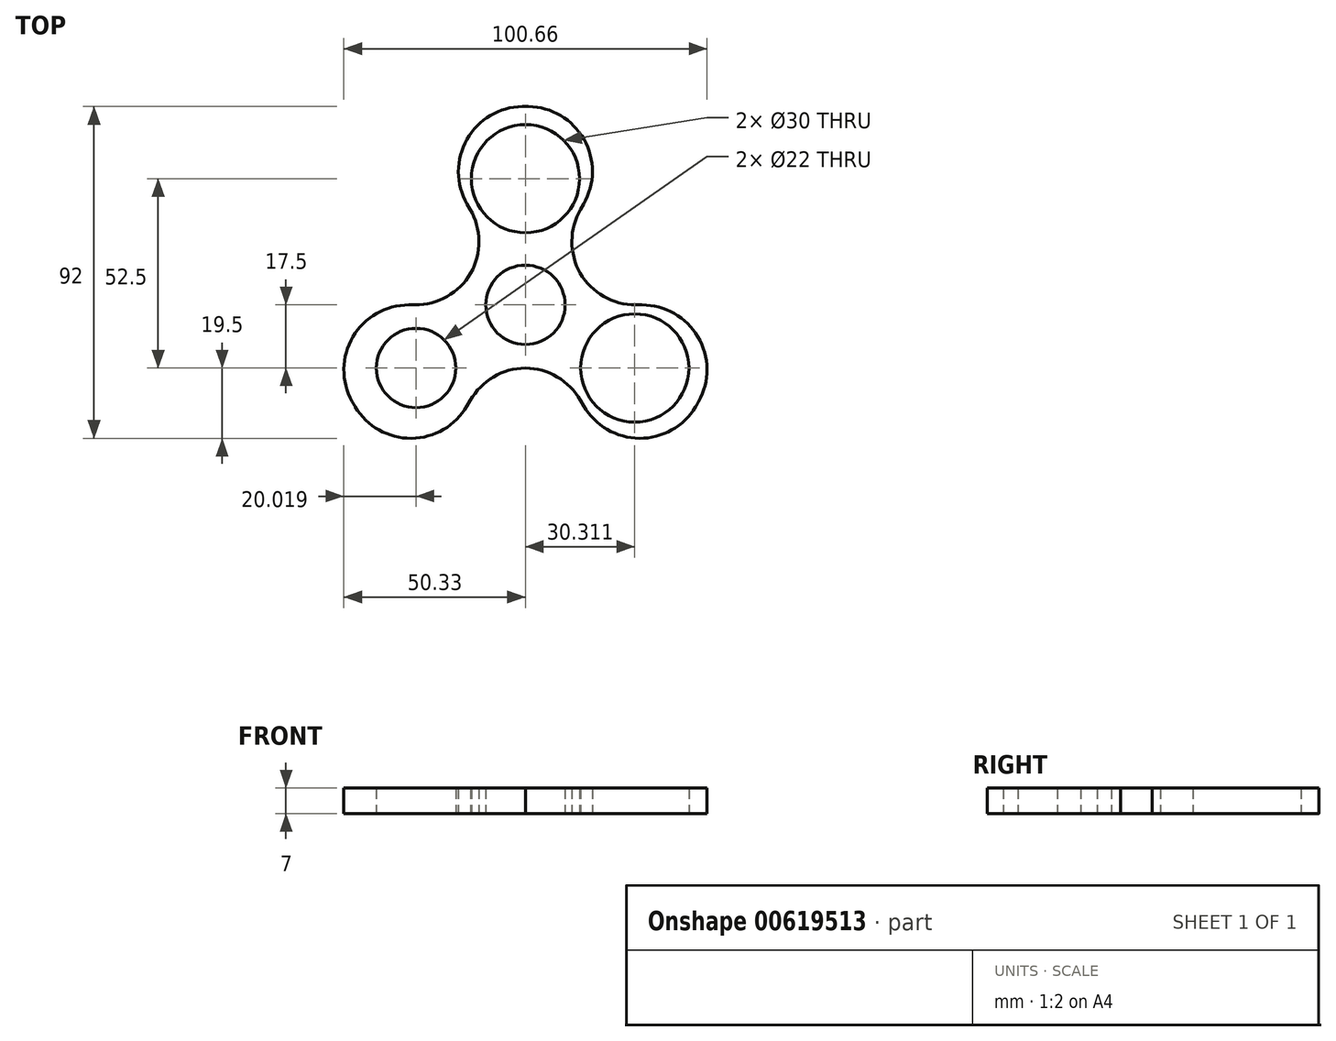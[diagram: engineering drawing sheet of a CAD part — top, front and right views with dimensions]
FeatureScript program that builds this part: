
annotation { "Feature Type Name" : "Feature", "Feature Type Description" : "" }
export const myFeature = defineFeature(function(context is Context, id is Id, definition is map)
    precondition{}
    {
        {
            var Q0;
            Q0=qCreatedBy(makeId("Top.planeOp"),FACE);
            var sketch = newSketch(context, id + "F0", { "sketchPlane" : qUnion([Q0])});
            skCircle(sketch, "E0", {"center": v(0, 0) * mm, "radius": 11 * mm});
            skCircle(sketch, "E1", {"center": v(0, 0) * mm, "radius": 15 * mm});
            skLineSegment(sketch, "E2", {"start": v(0, 11) * mm, "end": v(0, 55) * mm});
            skLineSegment(sketch, "E3.1.0", {"start": v(-5.5, 9.53) * mm, "end": v(-27.5, 47.63) * mm});
            skLineSegment(sketch, "E3.2.0", {"start": v(-9.53, 5.5) * mm, "end": v(-47.63, 27.5) * mm});
            skLineSegment(sketch, "E4.1.3.0", {"start": v(-11, 0) * mm, "end": v(-55, 0) * mm});
            skLineSegment(sketch, "E4.1.4.0", {"start": v(-9.53, -5.5) * mm, "end": v(-47.63, -27.5) * mm});
            skLineSegment(sketch, "E4.1.5.0", {"start": v(-5.5, -9.53) * mm, "end": v(-27.5, -47.63) * mm});
            skCircle(sketch, "E5", {"center": v(0, 0) * mm, "radius": 55 * mm});
            skLineSegment(sketch, "E6.1.6.0", {"start": v(0, -11) * mm, "end": v(0, -55) * mm});
            skLineSegment(sketch, "E6.1.7.0", {"start": v(5.5, -9.53) * mm, "end": v(27.5, -47.63) * mm});
            skLineSegment(sketch, "E6.1.8.0", {"start": v(9.53, -5.5) * mm, "end": v(47.63, -27.5) * mm});
            skLineSegment(sketch, "E6.1.9.0", {"start": v(11, 0) * mm, "end": v(55, 0) * mm});
            skLineSegment(sketch, "E6.1.10.0", {"start": v(9.53, 5.5) * mm, "end": v(47.63, 27.5) * mm});
            skLineSegment(sketch, "E6.1.11.0", {"start": v(5.5, 9.53) * mm, "end": v(27.5, 47.63) * mm});
            skCircle(sketch, "E7", {"center": v(-30.31, -17.5) * mm, "radius": 15 * mm});
            skCircle(sketch, "E8.1.0", {"center": v(30.31, -17.5) * mm, "radius": 15 * mm});
            skCircle(sketch, "E8.2.0", {"center": v(0, 35) * mm, "radius": 15 * mm});
            skCircle(sketch, "E9", {"center": v(-30.31, -17.5) * mm, "radius": 11 * mm});
            skCircle(sketch, "E10.1.0", {"center": v(30.31, -17.5) * mm, "radius": 11 * mm});
            skCircle(sketch, "E10.2.0", {"center": v(0, 35) * mm, "radius": 11 * mm});
            skCircle(sketch, "E11", {"center": v(0, 0) * mm, "radius": 17.5 * mm});
            skSolve(sketch);
        }
        {
            var Q0;
            Q0=makeQuery(id+"F0.imprint","IMPRINT",FACE,{"disambiguationData":[TD([[makeQuery(id+"F0.imprint","IMPRINT",EDGE,{"derivedFrom":sQuery(id+"F0.wireOp",EDGE,"E0")}),-1.0]])]});
            var Q1;
            {var subQ0=sQuery(id+"F0.wireOp",EDGE,"E4.1.5.0");var subQ1=sQuery(id+"F0.wireOp",EDGE,"E1");var subQ2=makeQuery(id+"F0.imprint","INTERSECT",VERTEX,{"derivedFrom":[subQ1,subQ0]});Q1=makeQuery(id+"F0.imprint","IMPRINT",FACE,{"disambiguationData":[TD([[makeQuery(id+"F0.imprint","IMPRINT",EDGE,{"disambiguationData":[TD([[subQ2,1.0]])],"derivedFrom":subQ1}),-1.0]])]});}
            var Q2;
            {var subQ0=sQuery(id+"F0.wireOp",EDGE,"E2");var subQ1=sQuery(id+"F0.wireOp",EDGE,"E1");var subQ2=makeQuery(id+"F0.imprint","INTERSECT",VERTEX,{"derivedFrom":[subQ1,subQ0]});Q2=makeQuery(id+"F0.imprint","IMPRINT",FACE,{"disambiguationData":[TD([[makeQuery(id+"F0.imprint","IMPRINT",EDGE,{"disambiguationData":[TD([[subQ2,-1.0]])],"derivedFrom":subQ1}),-1.0]])]});}
            var Q3;
            {var subQ0=sQuery(id+"F0.wireOp",EDGE,"E6.1.11.0");var subQ1=sQuery(id+"F0.wireOp",EDGE,"E1");var subQ2=makeQuery(id+"F0.imprint","INTERSECT",VERTEX,{"derivedFrom":[subQ1,subQ0]});Q3=makeQuery(id+"F0.imprint","IMPRINT",FACE,{"disambiguationData":[TD([[makeQuery(id+"F0.imprint","IMPRINT",EDGE,{"disambiguationData":[TD([[subQ2,-1.0]])],"derivedFrom":subQ1}),-1.0]])]});}
            var Q4;
            {var subQ0=sQuery(id+"F0.wireOp",EDGE,"E4.1.3.0");var subQ1=sQuery(id+"F0.wireOp",EDGE,"E1");var subQ2=makeQuery(id+"F0.imprint","INTERSECT",VERTEX,{"derivedFrom":[subQ1,subQ0]});Q4=makeQuery(id+"F0.imprint","IMPRINT",FACE,{"disambiguationData":[TD([[makeQuery(id+"F0.imprint","IMPRINT",EDGE,{"disambiguationData":[TD([[subQ2,-1.0]])],"derivedFrom":subQ1}),-1.0]])]});}
            var Q5;
            {var subQ0=sQuery(id+"F0.wireOp",EDGE,"E6.1.9.0");var subQ1=sQuery(id+"F0.wireOp",EDGE,"E1");var subQ2=makeQuery(id+"F0.imprint","INTERSECT",VERTEX,{"derivedFrom":[subQ1,subQ0]});Q5=makeQuery(id+"F0.imprint","IMPRINT",FACE,{"disambiguationData":[TD([[makeQuery(id+"F0.imprint","IMPRINT",EDGE,{"disambiguationData":[TD([[subQ2,1.0]])],"derivedFrom":subQ1}),-1.0]])]});}
            var Q6;
            {var subQ0=sQuery(id+"F0.wireOp",EDGE,"E6.1.7.0");var subQ1=sQuery(id+"F0.wireOp",EDGE,"E1");var subQ2=makeQuery(id+"F0.imprint","INTERSECT",VERTEX,{"derivedFrom":[subQ1,subQ0]});Q6=makeQuery(id+"F0.imprint","IMPRINT",FACE,{"disambiguationData":[TD([[makeQuery(id+"F0.imprint","IMPRINT",EDGE,{"disambiguationData":[TD([[subQ2,-1.0]])],"derivedFrom":subQ1}),-1.0]])]});}
            var Q7;
            {var subQ0=sQuery(id+"F0.wireOp",EDGE,"E7");var subQ1=sQuery(id+"F0.wireOp",EDGE,"E4.1.4.0");var subQ2=makeQuery(id+"F0.imprint","INTERSECT",VERTEX,{"disambiguationData":[OD(0.0)],"derivedFrom":[subQ1,subQ0]});Q7=makeQuery(id+"F0.imprint","IMPRINT",FACE,{"disambiguationData":[TD([[makeQuery(id+"F0.imprint","IMPRINT",EDGE,{"disambiguationData":[TD([[subQ2,-1.0]])],"derivedFrom":subQ1}),-1.0]])]});}
            var Q8;
            {var subQ0=sQuery(id+"F0.wireOp",EDGE,"E8.1.0");var subQ1=sQuery(id+"F0.wireOp",EDGE,"E6.1.8.0");var subQ2=makeQuery(id+"F0.imprint","INTERSECT",VERTEX,{"disambiguationData":[OD(0.0)],"derivedFrom":[subQ1,subQ0]});Q8=makeQuery(id+"F0.imprint","IMPRINT",FACE,{"disambiguationData":[TD([[makeQuery(id+"F0.imprint","IMPRINT",EDGE,{"disambiguationData":[TD([[subQ2,-1.0]])],"derivedFrom":subQ1}),1.0]])]});}
            var Q9;
            {var subQ0=sQuery(id+"F0.wireOp",EDGE,"E8.1.0");var subQ1=sQuery(id+"F0.wireOp",EDGE,"E6.1.8.0");var subQ2=makeQuery(id+"F0.imprint","INTERSECT",VERTEX,{"disambiguationData":[OD(0.0)],"derivedFrom":[subQ1,subQ0]});Q9=makeQuery(id+"F0.imprint","IMPRINT",FACE,{"disambiguationData":[TD([[makeQuery(id+"F0.imprint","IMPRINT",EDGE,{"disambiguationData":[TD([[subQ2,-1.0]])],"derivedFrom":subQ1}),-1.0]])]});}
            var Q10;
            {var subQ0=sQuery(id+"F0.wireOp",EDGE,"E8.2.0");var subQ1=sQuery(id+"F0.wireOp",EDGE,"E2");var subQ2=makeQuery(id+"F0.imprint","INTERSECT",VERTEX,{"disambiguationData":[OD(0.0)],"derivedFrom":[subQ1,subQ0]});Q10=makeQuery(id+"F0.imprint","IMPRINT",FACE,{"disambiguationData":[TD([[makeQuery(id+"F0.imprint","IMPRINT",EDGE,{"disambiguationData":[TD([[subQ2,-1.0]])],"derivedFrom":subQ1}),1.0]])]});}
            var Q11;
            {var subQ0=sQuery(id+"F0.wireOp",EDGE,"E8.2.0");var subQ1=sQuery(id+"F0.wireOp",EDGE,"E2");var subQ2=makeQuery(id+"F0.imprint","INTERSECT",VERTEX,{"disambiguationData":[OD(0.0)],"derivedFrom":[subQ1,subQ0]});Q11=makeQuery(id+"F0.imprint","IMPRINT",FACE,{"disambiguationData":[TD([[makeQuery(id+"F0.imprint","IMPRINT",EDGE,{"disambiguationData":[TD([[subQ2,-1.0]])],"derivedFrom":subQ1}),-1.0]])]});}
            var Q12;
            {var subQ0=sQuery(id+"F0.wireOp",EDGE,"E7");var subQ1=sQuery(id+"F0.wireOp",EDGE,"E4.1.4.0");var subQ2=makeQuery(id+"F0.imprint","INTERSECT",VERTEX,{"disambiguationData":[OD(0.0)],"derivedFrom":[subQ1,subQ0]});Q12=makeQuery(id+"F0.imprint","IMPRINT",FACE,{"disambiguationData":[TD([[makeQuery(id+"F0.imprint","IMPRINT",EDGE,{"disambiguationData":[TD([[subQ2,-1.0]])],"derivedFrom":subQ1}),1.0]])]});}
            var Q13;
            {var subQ1=sQuery(id+"F0.wireOp",EDGE,"E2");var subQ5=sQuery(id+"F0.wireOp",EDGE,"E11");var subQ7=makeQuery(id+"F0.imprint","INTERSECT",VERTEX,{"derivedFrom":[subQ1,subQ5]});Q13=makeQuery(id+"F0.imprint","IMPRINT",FACE,{"disambiguationData":[TD([[makeQuery(id+"F0.imprint","IMPRINT",EDGE,{"disambiguationData":[TD([[subQ7,-1.0]])],"derivedFrom":subQ1}),1.0]])]});}
            var Q14;
            {var subQ0=sQuery(id+"F0.wireOp",EDGE,"E3.1.0");var subQ1=sQuery(id+"F0.wireOp",EDGE,"E1");var subQ2=makeQuery(id+"F0.imprint","INTERSECT",VERTEX,{"derivedFrom":[subQ1,subQ0]});Q14=makeQuery(id+"F0.imprint","IMPRINT",FACE,{"disambiguationData":[TD([[makeQuery(id+"F0.imprint","IMPRINT",EDGE,{"disambiguationData":[TD([[subQ2,-1.0]])],"derivedFrom":subQ1}),-1.0]])]});}
            var Q15;
            {var subQ0=sQuery(id+"F0.wireOp",EDGE,"E5");var subQ1=sQuery(id+"F0.wireOp",EDGE,"E4.1.3.0");var subQ2=makeQuery(id+"F0.imprint","INTERSECT",VERTEX,{"derivedFrom":[subQ1,subQ0]});Q15=makeQuery(id+"F0.imprint","IMPRINT",FACE,{"disambiguationData":[TD([[makeQuery(id+"F0.imprint","IMPRINT",EDGE,{"disambiguationData":[TD([[subQ2,1.0]])],"derivedFrom":subQ1}),1.0]])]});}
            var Q16;
            {var subQ3=sQuery(id+"F0.wireOp",EDGE,"E11");var subQ5=sQuery(id+"F0.wireOp",EDGE,"E4.1.4.0");var subQ9=makeQuery(id+"F0.imprint","INTERSECT",VERTEX,{"derivedFrom":[subQ5,subQ3]});Q16=makeQuery(id+"F0.imprint","IMPRINT",FACE,{"disambiguationData":[TD([[makeQuery(id+"F0.imprint","IMPRINT",EDGE,{"disambiguationData":[TD([[subQ9,-1.0]])],"derivedFrom":subQ5}),1.0]])]});}
            var Q17;
            {var subQ0=sQuery(id+"F0.wireOp",EDGE,"E4.1.5.0");var subQ1=sQuery(id+"F0.wireOp",EDGE,"E1");var subQ2=makeQuery(id+"F0.imprint","INTERSECT",VERTEX,{"derivedFrom":[subQ1,subQ0]});Q17=makeQuery(id+"F0.imprint","IMPRINT",FACE,{"disambiguationData":[TD([[makeQuery(id+"F0.imprint","IMPRINT",EDGE,{"disambiguationData":[TD([[subQ2,-1.0]])],"derivedFrom":subQ1}),-1.0]])]});}
            var Q18;
            {var subQ0=sQuery(id+"F0.wireOp",EDGE,"E6.1.6.0");var subQ1=sQuery(id+"F0.wireOp",EDGE,"E1");var subQ2=makeQuery(id+"F0.imprint","INTERSECT",VERTEX,{"derivedFrom":[subQ1,subQ0]});Q18=makeQuery(id+"F0.imprint","IMPRINT",FACE,{"disambiguationData":[TD([[makeQuery(id+"F0.imprint","IMPRINT",EDGE,{"disambiguationData":[TD([[subQ2,-1.0]])],"derivedFrom":subQ1}),-1.0]])]});}
            var Q19;
            {var subQ1=sQuery(id+"F0.wireOp",EDGE,"E5");var subQ5=sQuery(id+"F0.wireOp",EDGE,"E6.1.7.0");var subQ6=makeQuery(id+"F0.imprint","INTERSECT",VERTEX,{"derivedFrom":[subQ1,subQ5]});Q19=makeQuery(id+"F0.imprint","IMPRINT",FACE,{"disambiguationData":[TD([[makeQuery(id+"F0.imprint","IMPRINT",EDGE,{"disambiguationData":[TD([[subQ6,-1.0]])],"derivedFrom":subQ1}),1.0]])]});}
            var Q20;
            {var subQ0=sQuery(id+"F0.wireOp",EDGE,"E3.2.0");var subQ1=sQuery(id+"F0.wireOp",EDGE,"E1");var subQ2=makeQuery(id+"F0.imprint","INTERSECT",VERTEX,{"derivedFrom":[subQ1,subQ0]});Q20=makeQuery(id+"F0.imprint","IMPRINT",FACE,{"disambiguationData":[TD([[makeQuery(id+"F0.imprint","IMPRINT",EDGE,{"disambiguationData":[TD([[subQ2,-1.0]])],"derivedFrom":subQ1}),-1.0]])]});}
            var Q21;
            {var subQ3=sQuery(id+"F0.wireOp",EDGE,"E11");var subQ5=sQuery(id+"F0.wireOp",EDGE,"E2");var subQ9=makeQuery(id+"F0.imprint","INTERSECT",VERTEX,{"derivedFrom":[subQ5,subQ3]});Q21=makeQuery(id+"F0.imprint","IMPRINT",FACE,{"disambiguationData":[TD([[makeQuery(id+"F0.imprint","IMPRINT",EDGE,{"disambiguationData":[TD([[subQ9,-1.0]])],"derivedFrom":subQ5}),-1.0]])]});}
            var Q22;
            {var subQ1=sQuery(id+"F0.wireOp",EDGE,"E5");var subQ5=sQuery(id+"F0.wireOp",EDGE,"E6.1.8.0");var subQ6=makeQuery(id+"F0.imprint","INTERSECT",VERTEX,{"derivedFrom":[subQ1,subQ5]});Q22=makeQuery(id+"F0.imprint","IMPRINT",FACE,{"disambiguationData":[TD([[makeQuery(id+"F0.imprint","IMPRINT",EDGE,{"disambiguationData":[TD([[subQ6,-1.0]])],"derivedFrom":subQ1}),1.0]])]});}
            var Q23;
            {var subQ0=sQuery(id+"F0.wireOp",EDGE,"E6.1.10.0");var subQ1=sQuery(id+"F0.wireOp",EDGE,"E1");var subQ2=makeQuery(id+"F0.imprint","INTERSECT",VERTEX,{"derivedFrom":[subQ1,subQ0]});Q23=makeQuery(id+"F0.imprint","IMPRINT",FACE,{"disambiguationData":[TD([[makeQuery(id+"F0.imprint","IMPRINT",EDGE,{"disambiguationData":[TD([[subQ2,-1.0]])],"derivedFrom":subQ1}),-1.0]])]});}
            var Q24;
            {var subQ0=sQuery(id+"F0.wireOp",EDGE,"E6.1.10.0");var subQ1=sQuery(id+"F0.wireOp",EDGE,"E1");var subQ2=makeQuery(id+"F0.imprint","INTERSECT",VERTEX,{"derivedFrom":[subQ1,subQ0]});Q24=makeQuery(id+"F0.imprint","IMPRINT",FACE,{"disambiguationData":[TD([[makeQuery(id+"F0.imprint","IMPRINT",EDGE,{"disambiguationData":[TD([[subQ2,1.0]])],"derivedFrom":subQ1}),-1.0]])]});}
            extrude(context, id + "F1", {"entities" : qUnion([Q0, Q1, Q2, Q3, Q4, Q5, Q6, Q7, Q8, Q9, Q10, Q11, Q12, Q13, Q14, Q15, Q16, Q17, Q18, Q19, Q20, Q21, Q22, Q23, Q24]), "depth" : 7 * mm, "offsetDistance" : 25 * mm});
        }
        {
            var Q0;
            Q0=makeQuery(id+"F1.opExtrude","SWEPT_EDGE",EDGE,{"disambiguationData":[OSD([sQuery(id+"F0.wireOp",EDGE,"E4.1.5.0"),sQuery(id+"F0.wireOp",EDGE,"E5")])]});
            var Q1;
            Q1=makeQuery(id+"F1.opExtrude","SWEPT_EDGE",EDGE,{"disambiguationData":[OSD([sQuery(id+"F0.wireOp",EDGE,"E5"),sQuery(id+"F0.wireOp",EDGE,"E6.1.7.0")])]});
            var Q2;
            Q2=makeQuery(id+"F1.opExtrude","SWEPT_EDGE",EDGE,{"disambiguationData":[OSD([sQuery(id+"F0.wireOp",EDGE,"E5"),sQuery(id+"F0.wireOp",EDGE,"E6.1.9.0")])]});
            var Q3;
            Q3=makeQuery(id+"F1.opExtrude","SWEPT_EDGE",EDGE,{"disambiguationData":[OSD([sQuery(id+"F0.wireOp",EDGE,"E5"),sQuery(id+"F0.wireOp",EDGE,"E6.1.11.0")])]});
            var Q4;
            Q4=makeQuery(id+"F1.opExtrude","SWEPT_EDGE",EDGE,{"disambiguationData":[OSD([sQuery(id+"F0.wireOp",EDGE,"E4.1.3.0"),sQuery(id+"F0.wireOp",EDGE,"E5")])]});
            var Q5;
            Q5=makeQuery(id+"F1.opExtrude","SWEPT_EDGE",EDGE,{"disambiguationData":[OSD([sQuery(id+"F0.wireOp",EDGE,"E3.1.0"),sQuery(id+"F0.wireOp",EDGE,"E5")])]});
            fillet(context, id + "F2", {"entities" : qUnion([Q0, Q1, Q2, Q3, Q4, Q5]), "radius" : 18 * mm, "tangentPropagation" : true, "allowEdgeOverflow" : false});
        }
        {
            var Q0;
            Q0=makeQuery(id+"F1.opExtrude","SWEPT_EDGE",EDGE,{"disambiguationData":[OSD([sQuery(id+"F0.wireOp",EDGE,"E6.1.9.0"),sQuery(id+"F0.wireOp",EDGE,"E11")])]});
            var Q1;
            Q1=makeQuery(id+"F1.opExtrude","SWEPT_EDGE",EDGE,{"disambiguationData":[OSD([sQuery(id+"F0.wireOp",EDGE,"E6.1.11.0"),sQuery(id+"F0.wireOp",EDGE,"E11")])]});
            var Q2;
            Q2=makeQuery(id+"F1.opExtrude","SWEPT_EDGE",EDGE,{"disambiguationData":[OSD([sQuery(id+"F0.wireOp",EDGE,"E4.1.5.0"),sQuery(id+"F0.wireOp",EDGE,"E11")])]});
            var Q3;
            Q3=makeQuery(id+"F1.opExtrude","SWEPT_EDGE",EDGE,{"disambiguationData":[OSD([sQuery(id+"F0.wireOp",EDGE,"E6.1.7.0"),sQuery(id+"F0.wireOp",EDGE,"E11")])]});
            var Q4;
            Q4=makeQuery(id+"F1.opExtrude","SWEPT_EDGE",EDGE,{"disambiguationData":[OSD([sQuery(id+"F0.wireOp",EDGE,"E3.1.0"),sQuery(id+"F0.wireOp",EDGE,"E11")])]});
            var Q5;
            Q5=makeQuery(id+"F1.opExtrude","SWEPT_EDGE",EDGE,{"disambiguationData":[OSD([sQuery(id+"F0.wireOp",EDGE,"E4.1.3.0"),sQuery(id+"F0.wireOp",EDGE,"E11")])]});
            fillet(context, id + "F3", {"entities" : qUnion([Q0, Q1, Q2, Q3, Q4, Q5]), "radius" : 18 * mm, "tangentPropagation" : true, "allowEdgeOverflow" : false});
        }
    });
